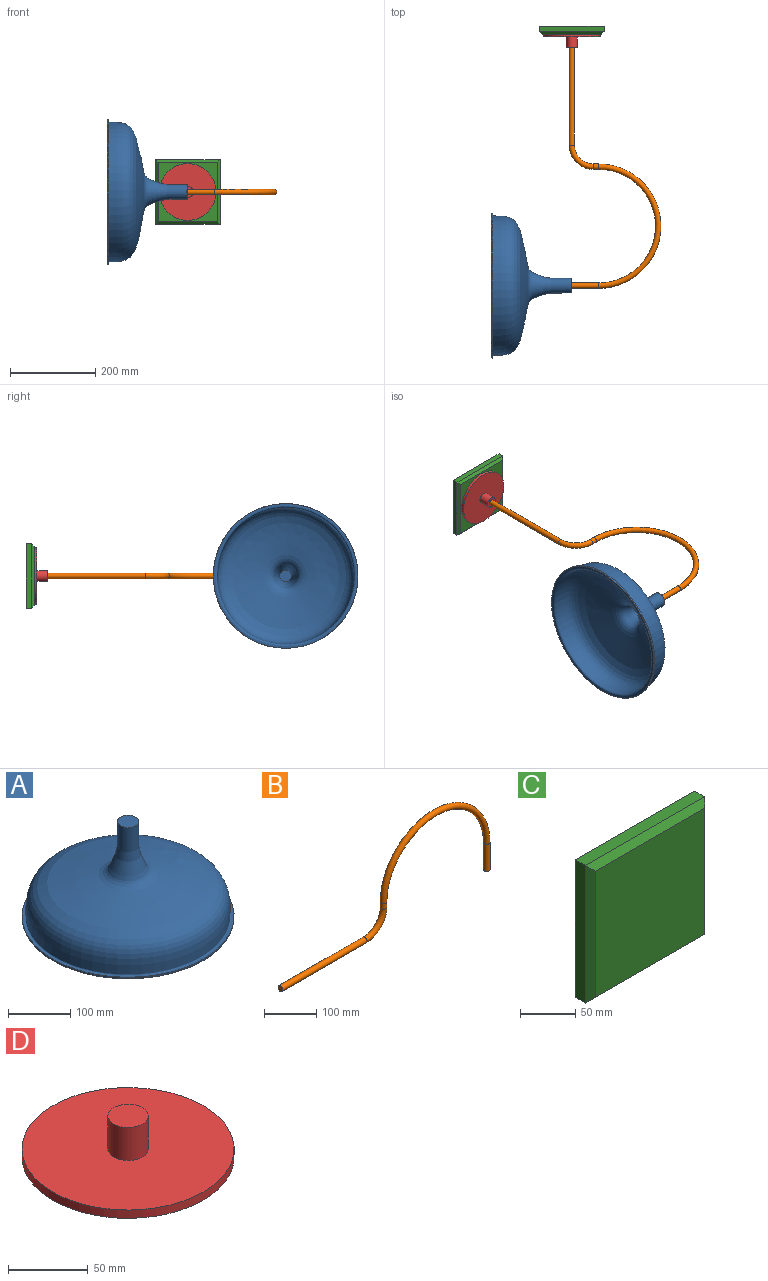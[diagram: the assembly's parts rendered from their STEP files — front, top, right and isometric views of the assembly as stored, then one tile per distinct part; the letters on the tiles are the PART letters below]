
ASSEMBLY  parts=4 mates=3
PART A: 5 faces, bbox 339.9x339.9x189.1 mm
  f0: revolved ~339.57x339.57mm, area 148009.1mm2, adj f1,f4
  f1: plane 27.86x27.86mm, normal (0,0,-1), area 609.4mm2, adj f0
  f2: plane 34.11x34.11mm, normal (0,0,1), area 913.7mm2, adj f3
  f3: revolved ~339.89x339.89mm, area 148164mm2, adj f2,f4
  f4: cone r=169.94mm half-angle=2.9deg, axis (0,0,1), area 3388.7mm2, adj f0,f3
PART B: 7 faces, bbox 577.2x12.7x232.5 mm
  f0: plane 12.7x12.7mm, normal (-1,0,0), area 126.7mm2, adj f2
  f1: plane 12.7x12.7mm, normal (0,0,-1), area 126.7mm2, adj f6
  f2: cylinder r=6.35mm len=228.6mm, axis (1,0,0), area 9120.7mm2, adj f0,f3
  f3: torus R=50.8mm, axis (0,-1,0), area 3183.7mm2, adj f2,f4
  f4: cylinder r=6.35mm len=12.7mm, axis (0,0,1), area 499.9mm2, adj f3,f5
  f5: torus R=139.7mm, axis (0,1,0), area 17510.6mm2, adj f4,f6
  f6: cylinder r=6.35mm len=63.5mm, axis (0,0,-1), area 2533.5mm2, adj f1,f5
PART C: 10 faces, bbox 152.4x19.1x152.4 mm
  f0: plane 152.4x12.7mm, normal (1,0,0), area 1935.5mm2, adj f1,f3,f5,f7
  f1: plane 152.4x12.7mm, normal (0,0,1), area 1935.5mm2, adj f0,f2,f5,f9
  f2: plane 152.4x12.7mm, normal (-1,0,0), area 1935.5mm2, adj f1,f3,f5,f8
  f3: plane 152.4x12.7mm, normal (0,0,-1), area 1935.5mm2, adj f0,f2,f5,f6
  f4: plane 139.7x139.7mm, normal (0,-1,0), area 19516.1mm2, adj f6,f7,f8,f9
  f5: plane 152.4x152.4mm, normal (0,1,0), area 23225.8mm2, adj f0,f1,f2,f3
  f6: plane 152.4x6.35mm, normal (0,-0.71,-0.71), area 1311.6mm2, adj f3,f4,f7,f8
  f7: plane 152.4x6.35mm, normal (0.71,-0.71,0), area 1311.6mm2, adj f0,f4,f6,f9
  f8: plane 152.4x6.35mm, normal (-0.71,-0.71,0), area 1311.6mm2, adj f2,f4,f6,f9
  f9: plane 152.4x6.35mm, normal (0,-0.71,0.71), area 1311.6mm2, adj f1,f4,f7,f8
PART D: 5 faces, bbox 133.4x133.4x31.8 mm
  f0: plane 25.4x25.4mm, normal (0,0,1), area 506.7mm2, adj f1
  f1: cylinder r=12.7mm len=25.4mm, axis (0,0,1), area 2026.8mm2, adj f0,f2
  f2: plane 133.35x133.35mm, normal (0,0,1), area 13459.4mm2, adj f1,f3
  f3: cylinder r=66.67mm len=133.35mm, axis (0,0,1), area 2660.2mm2, adj f2,f4
  f4: plane 133.35x133.35mm, normal (0,0,-1), area 13966.1mm2, adj f3
PLACE A rot(axis=(0,1,0),90deg) t=(-887.39,-926.29,195.63)mm
PLACE B rot(axis=(-0.58,0.58,-0.58),120deg) t=(-829.78,-1508.37,195.63)mm
PLACE C t=(190.71,-316.69,265.13)mm
PLACE D rot(axis=(1,0,0),90deg) t=(-292.78,-486.16,195.63)mm
MATE fastened A.f4 <-> B.f6  axis (1,0,0) through (-791.09,-926.29,195.63)mm
MATE fastened B.f2 <-> D.f1  axis (0,1,0) through (-790.92,-367.49,195.63)mm
MATE fastened D.f1 <-> C.f4  axis (0,1,0) through (-790.92,-335.74,195.63)mm
